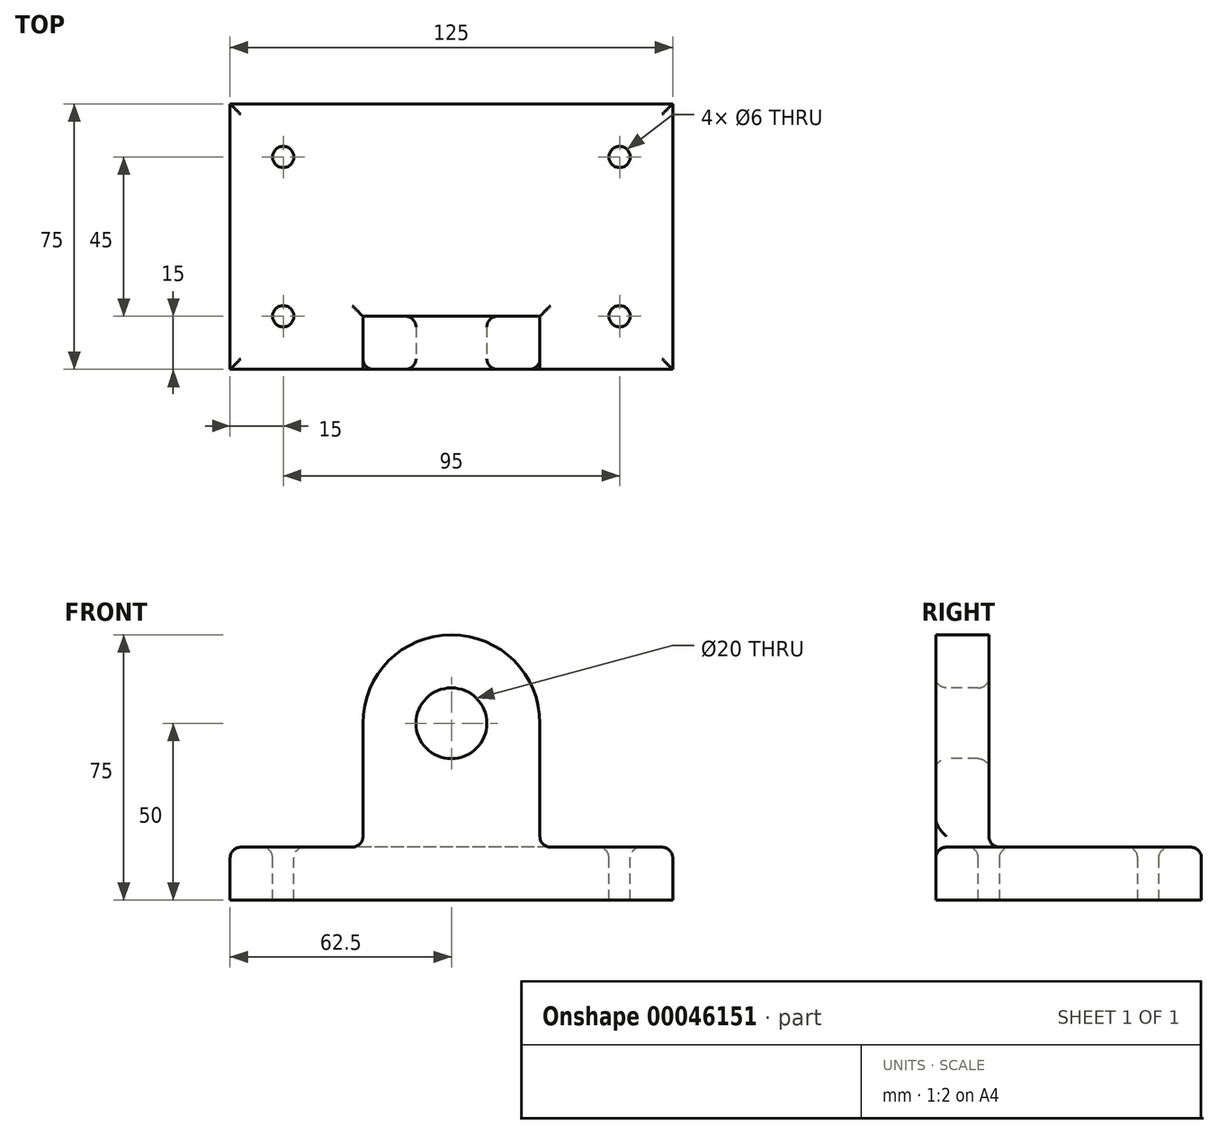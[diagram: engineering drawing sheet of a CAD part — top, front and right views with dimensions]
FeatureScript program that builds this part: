
annotation { "Feature Type Name" : "Feature", "Feature Type Description" : "" }
export const myFeature = defineFeature(function(context is Context, id is Id, definition is map)
    precondition{}
    {
        {
            var Q0;
            Q0=qCreatedBy(makeId("Top.planeOp"),FACE);
            var sketch = newSketch(context, id + "F0", { "sketchPlane" : qUnion([Q0])});
            skLineSegment(sketch, "E0.rect.bottom", {"start": v(62.5, -37.5) * mm, "end": v(-62.5, -37.5) * mm});
            skLineSegment(sketch, "E0.rect.top", {"start": v(62.5, 37.5) * mm, "end": v(-62.5, 37.5) * mm});
            skLineSegment(sketch, "E0.rect.left", {"start": v(62.5, -37.5) * mm, "end": v(62.5, 37.5) * mm});
            skLineSegment(sketch, "E0.rect.right", {"start": v(-62.5, -37.5) * mm, "end": v(-62.5, 37.5) * mm});
            skPoint(sketch, "E0.rect.middle", {"position": v(0, 0) * mm});
            skSolve(sketch);
        }
        {
            var Q0;
            Q0=makeQuery(id+"F0.imprint","IMPRINT",FACE,{"disambiguationData":[TD([[makeQuery(id+"F0.imprint","IMPRINT",EDGE,{"derivedFrom":sQuery(id+"F0.wireOp",EDGE,"E0.rect.bottom")}),-1.0]])]});
            extrude(context, id + "F1", {"entities" : qUnion([Q0]), "depth" : 15 * mm});
        }
        {
            var Q0;
            Q0=makeQuery(id+"F1.opExtrude","SWEPT_FACE",FACE,{"disambiguationData":[OSD([sQuery(id+"F0.wireOp",EDGE,"E0.rect.bottom")])]});
            var sketch = newSketch(context, id + "F2", { "sketchPlane" : qUnion([Q0])});
            skLineSegment(sketch, "E1", {"start": v(0, 0) * mm, "end": v(0, 50) * mm, "construction": true});
            skCircle(sketch, "E2", {"center": v(0, 50) * mm, "radius": 25 * mm});
            skLineSegment(sketch, "E3.rect.left", {"start": v(-25, 50) * mm, "end": v(-25, 50) * mm});
            skLineSegment(sketch, "E3.rect.right", {"start": v(25, 50) * mm, "end": v(25, 50) * mm});
            skLineSegment(sketch, "E4.bottom", {"start": v(-25, 50) * mm, "end": v(25, 50) * mm});
            skLineSegment(sketch, "E4.top", {"start": v(-25, 0) * mm, "end": v(25, 0) * mm});
            skLineSegment(sketch, "E4.left", {"start": v(-25, 50) * mm, "end": v(-25, 0) * mm});
            skLineSegment(sketch, "E4.right", {"start": v(25, 50) * mm, "end": v(25, 0) * mm});
            skCircle(sketch, "E5", {"center": v(0, 50) * mm, "radius": 10 * mm});
            skSolve(sketch);
        }
        {
            var Q0;
            {var subQ0=sQuery(id+"F2.wireOp",EDGE,"E4.bottom");var subQ1=sQuery(id+"F2.wireOp",EDGE,"E5");var subQ5=makeQuery(id+"F2.imprint","INTERSECT",VERTEX,{"disambiguationData":[OD(0.0)],"derivedFrom":[subQ0,subQ1]});Q0=makeQuery(id+"F2.imprint","IMPRINT",FACE,{"disambiguationData":[TD([[makeQuery(id+"F2.imprint","IMPRINT",EDGE,{"disambiguationData":[TD([[subQ5,1.0]])],"derivedFrom":subQ1}),-1.0]])]});}
            var Q1;
            {var subQ0=sQuery(id+"F2.wireOp",EDGE,"E4.bottom");var subQ1=sQuery(id+"F2.wireOp",EDGE,"E5");var subQ5=makeQuery(id+"F2.imprint","INTERSECT",VERTEX,{"disambiguationData":[OD(0.0)],"derivedFrom":[subQ0,subQ1]});Q1=makeQuery(id+"F2.imprint","IMPRINT",FACE,{"disambiguationData":[TD([[makeQuery(id+"F2.imprint","IMPRINT",EDGE,{"disambiguationData":[TD([[subQ5,-1.0]])],"derivedFrom":subQ1}),-1.0]])]});}
            var Q2;
            {var subQ0=sQuery(id+"F2.wireOp",EDGE,"E4.left");var subQ1=makeQuery(id+"F1.opExtrude","CAP_EDGE",EDGE,{"disambiguationData":[OSD([sQuery(id+"F0.wireOp",EDGE,"E0.rect.bottom")])],"isStart":false});var subQ2=makeQuery(id+"F2.imprint","INTERSECT",VERTEX,{"derivedFrom":[subQ1,subQ0]});Q2=makeQuery(id+"F2.imprint","IMPRINT",FACE,{"disambiguationData":[TD([[makeQuery(id+"F2.imprint","IMPRINT",EDGE,{"disambiguationData":[TD([[subQ2,1.0]])],"derivedFrom":subQ1}),-1.0]])]});}
            extrude(context, id + "F3", {"entities" : qUnion([Q0, Q1, Q2]), "operationType" : NewBodyOperationType.ADD, "oppositeDirection" : true, "depth" : 15 * mm});
        }
        {
            var Q0;
            Q0=makeQuery(id+"F1.opExtrude","CAP_FACE",FACE,{"disambiguationData":[OSD([sQuery(id+"F0.wireOp",EDGE,"E0.rect.bottom"),sQuery(id+"F0.wireOp",EDGE,"E0.rect.top"),sQuery(id+"F0.wireOp",EDGE,"E0.rect.left"),sQuery(id+"F0.wireOp",EDGE,"E0.rect.right")])],"isStart":false});
            var sketch = newSketch(context, id + "F4", { "sketchPlane" : qUnion([Q0])});
            skLineSegment(sketch, "E6.rect.bottom", {"start": v(-47.5, -22.5) * mm, "end": v(47.5, -22.5) * mm, "construction": true});
            skLineSegment(sketch, "E6.rect.top", {"start": v(-47.5, 22.5) * mm, "end": v(47.5, 22.5) * mm, "construction": true});
            skLineSegment(sketch, "E6.rect.left", {"start": v(-47.5, -22.5) * mm, "end": v(-47.5, 22.5) * mm, "construction": true});
            skLineSegment(sketch, "E6.rect.right", {"start": v(47.5, -22.5) * mm, "end": v(47.5, 22.5) * mm, "construction": true});
            skPoint(sketch, "E6.rect.middle", {"position": v(0, 0) * mm});
            skCircle(sketch, "E7", {"center": v(-47.5, 22.5) * mm, "radius": 3 * mm});
            skCircle(sketch, "E8", {"center": v(-47.5, -22.5) * mm, "radius": 3 * mm});
            skCircle(sketch, "E9", {"center": v(47.5, 22.5) * mm, "radius": 3 * mm});
            skCircle(sketch, "E10", {"center": v(47.5, -22.5) * mm, "radius": 3 * mm});
            skSolve(sketch);
        }
        {
            var Q0;
            Q0=makeQuery(id+"F4.imprint","IMPRINT",FACE,{"disambiguationData":[TD([[makeQuery(id+"F4.imprint","IMPRINT",EDGE,{"derivedFrom":sQuery(id+"F4.wireOp",EDGE,"E7")}),1.0]])]});
            var Q1;
            Q1=makeQuery(id+"F4.imprint","IMPRINT",FACE,{"disambiguationData":[TD([[makeQuery(id+"F4.imprint","IMPRINT",EDGE,{"derivedFrom":sQuery(id+"F4.wireOp",EDGE,"E8")}),1.0]])]});
            var Q2;
            Q2=makeQuery(id+"F4.imprint","IMPRINT",FACE,{"disambiguationData":[TD([[makeQuery(id+"F4.imprint","IMPRINT",EDGE,{"derivedFrom":sQuery(id+"F4.wireOp",EDGE,"E9")}),1.0]])]});
            var Q3;
            Q3=makeQuery(id+"F4.imprint","IMPRINT",FACE,{"disambiguationData":[TD([[makeQuery(id+"F4.imprint","IMPRINT",EDGE,{"derivedFrom":sQuery(id+"F4.wireOp",EDGE,"E10")}),1.0]])]});
            extrude(context, id + "F5", {"entities" : qUnion([Q0, Q1, Q2, Q3]), "operationType" : NewBodyOperationType.REMOVE, "oppositeDirection" : true, "depth" : 25 * mm});
        }
        {
            var Q0;
            Q0=makeQuery(id+"F1.opExtrude","CAP_FACE",FACE,{"disambiguationData":[OSD([sQuery(id+"F0.wireOp",EDGE,"E0.rect.bottom"),sQuery(id+"F0.wireOp",EDGE,"E0.rect.top"),sQuery(id+"F0.wireOp",EDGE,"E0.rect.left"),sQuery(id+"F0.wireOp",EDGE,"E0.rect.right")])],"isStart":false});
            var Q1;
            Q1=makeQuery(id+"F3.opExtrude","CAP_EDGE",EDGE,{"disambiguationData":[OSD([sQuery(id+"F2.wireOp",EDGE,"E5")])],"isStart":true});
            var Q2;
            Q2=makeQuery(id+"F3.opExtrude","CAP_EDGE",EDGE,{"disambiguationData":[OSD([sQuery(id+"F2.wireOp",EDGE,"E5")])],"isStart":false});
            fillet(context, id + "F6", {"entities" : qUnion([Q0, Q1, Q2]), "radius" : 3 * mm, "tangentPropagation" : true, "allowEdgeOverflow" : false});
        }
    });
